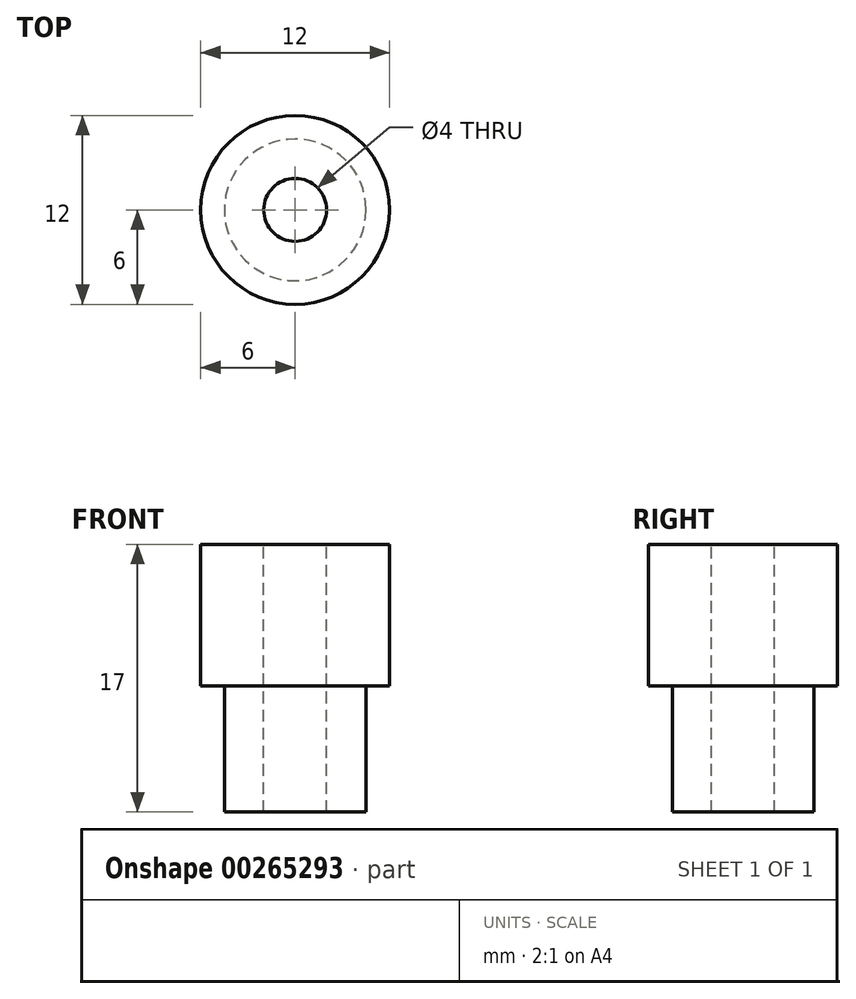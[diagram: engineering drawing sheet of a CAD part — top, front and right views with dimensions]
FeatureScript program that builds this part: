
annotation { "Feature Type Name" : "Feature", "Feature Type Description" : "" }
export const myFeature = defineFeature(function(context is Context, id is Id, definition is map)
    precondition{}
    {
        {
            var Q0;
            Q0=qCreatedBy(makeId("Right.planeOp"),FACE);
            var sketch = newSketch(context, id + "F0", { "sketchPlane" : qUnion([Q0])});
            skLineSegment(sketch, "E0", {"start": v(0, 0) * mm, "end": v(-2, 0) * mm, "construction": true});
            skLineSegment(sketch, "E1", {"start": v(-2, 0) * mm, "end": v(-6, 0) * mm});
            skLineSegment(sketch, "E2", {"start": v(-6, 0) * mm, "end": v(-6, -9) * mm});
            skLineSegment(sketch, "E3", {"start": v(-6, -9) * mm, "end": v(-4.5, -9) * mm});
            skLineSegment(sketch, "E4", {"start": v(-4.5, -9) * mm, "end": v(-4.5, -17) * mm});
            skLineSegment(sketch, "E5", {"start": v(-4.5, -17) * mm, "end": v(-2, -17) * mm});
            skLineSegment(sketch, "E6", {"start": v(-2, -17) * mm, "end": v(-2, 0) * mm});
            skLineSegment(sketch, "E7", {"start": v(0, 0) * mm, "end": v(0, -18.21) * mm, "construction": true});
            skSolve(sketch);
        }
        {
            var Q0;
            Q0=makeQuery(id+"F0.imprint","IMPRINT",FACE,{"disambiguationData":[TD([[makeQuery(id+"F0.imprint","IMPRINT",EDGE,{"derivedFrom":sQuery(id+"F0.wireOp",EDGE,"E1")}),1.0]])]});
            var Q1;
            Q1=sQuery(id+"F0.wireOp",EDGE,"E7");
            revolve(context, id + "F1", {"entities" : qUnion([Q0]), "axis" : qUnion([Q1]), "revolveType" : RevolveType.FULL});
        }
    });
